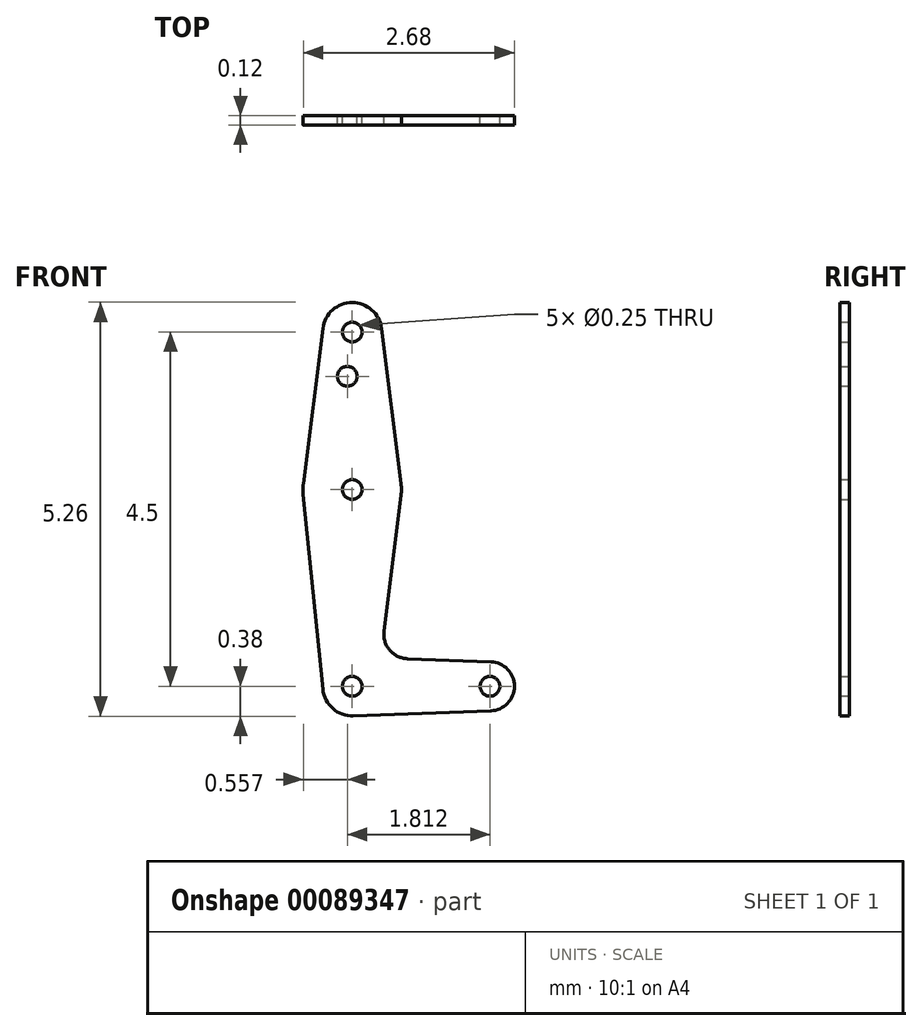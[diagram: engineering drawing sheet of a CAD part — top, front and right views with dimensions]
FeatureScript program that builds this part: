
annotation { "Feature Type Name" : "Feature", "Feature Type Description" : "" }
export const myFeature = defineFeature(function(context is Context, id is Id, definition is map)
    precondition{}
    {
        {
            var Q0;
            Q0=qCreatedBy(makeId("Front.planeOp"),FACE);
            var sketch = newSketch(context, id + "F0", { "sketchPlane" : qUnion([Q0])});
            skCircle(sketch, "E0", {"center": v(0, 0) * mm, "radius": 0.38 * mm});
            skCircle(sketch, "E1", {"center": v(0, 4.5) * mm, "radius": 0.38 * mm});
            skLineSegment(sketch, "E2", {"start": v(0, 0) * mm, "end": v(0, 4.5) * mm, "construction": true});
            skCircle(sketch, "E3", {"center": v(0, 2.5) * mm, "radius": 0.62 * mm});
            skCircle(sketch, "E4", {"center": v(1.75, 0) * mm, "radius": 0.31 * mm});
            skLineSegment(sketch, "E5", {"start": v(0, 0) * mm, "end": v(1.75, 0) * mm, "construction": true});
            skLineSegment(sketch, "E6", {"start": v(-0.37, 4.55) * mm, "end": v(-0.62, 2.58) * mm});
            skLineSegment(sketch, "E7", {"start": v(0.37, 4.55) * mm, "end": v(0.62, 2.58) * mm});
            skLineSegment(sketch, "E8", {"start": v(0.7, 0.35) * mm, "end": v(1.76, 0.31) * mm});
            skLineSegment(sketch, "E9", {"start": v(0, -0.38) * mm, "end": v(1.76, -0.31) * mm});
            skLineSegment(sketch, "E10", {"start": v(0.62, 2.42) * mm, "end": v(0.4, 0.7) * mm});
            skCircle(sketch, "E11", {"center": v(-0.06, 3.94) * mm, "radius": 0.12 * mm});
            skCircle(sketch, "E12", {"center": v(0, 4.5) * mm, "radius": 0.12 * mm});
            skCircle(sketch, "E13", {"center": v(0, 2.5) * mm, "radius": 0.12 * mm});
            skCircle(sketch, "E14", {"center": v(0, 0) * mm, "radius": 0.12 * mm});
            skCircle(sketch, "E15", {"center": v(1.75, 0) * mm, "radius": 0.12 * mm});
            skArc(sketch, "E16.filletArc", {"start": v(0.4, 0.7) * mm, "mid": v(0.48, 0.46) * mm, "end": v(0.7, 0.35) * mm});
            skLineSegment(sketch, "E17", {"start": v(-0.62, 2.44) * mm, "end": v(-0.37, -0.04) * mm});
            skSolve(sketch);
        }
        {
            var Q0;
            Q0 = qSketchRegion(id + "F0", true);
            extrude(context, id + "F1", {"entities" : qUnion([Q0]), "depth" : 0.12 * mm});
        }
    });
